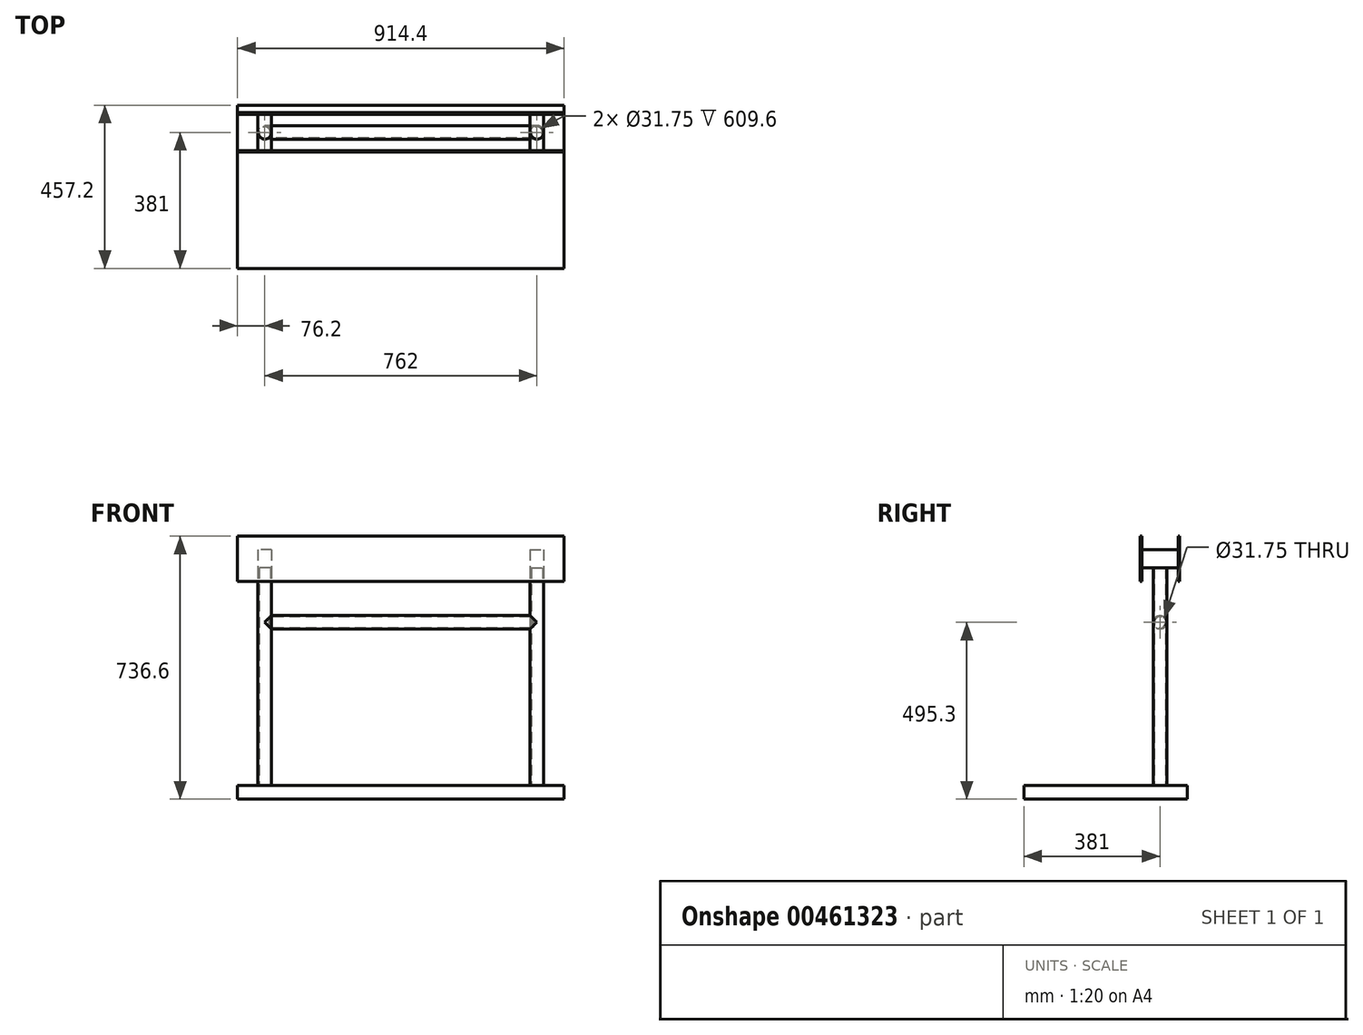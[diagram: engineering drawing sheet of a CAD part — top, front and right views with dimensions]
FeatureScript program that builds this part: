
annotation { "Feature Type Name" : "Feature", "Feature Type Description" : "" }
export const myFeature = defineFeature(function(context is Context, id is Id, definition is map)
    precondition{}
    {
        {
            var Q0;
            Q0=qCreatedBy(makeId("Top.planeOp"),FACE);
            var sketch = newSketch(context, id + "F0", { "sketchPlane" : qUnion([Q0])});
            skLineSegment(sketch, "E0.bottom", {"start": v(457.2, 228.6) * mm, "end": v(-457.2, 228.6) * mm});
            skLineSegment(sketch, "E0.top", {"start": v(457.2, -228.6) * mm, "end": v(-457.2, -228.6) * mm});
            skLineSegment(sketch, "E0.left", {"start": v(457.2, 228.6) * mm, "end": v(457.2, -228.6) * mm});
            skLineSegment(sketch, "E0.right", {"start": v(-457.2, 228.6) * mm, "end": v(-457.2, -228.6) * mm});
            skPoint(sketch, "E0.middle", {"position": v(0, 0) * mm});
            skSolve(sketch);
        }
        {
            var Q0;
            Q0 = qSketchRegion(id + "F0", true);
            extrude(context, id + "F1", {"entities" : qUnion([Q0]), "oppositeDirection" : true, "depth" : 38.1 * mm, "offsetDistance" : 25.4 * mm});
        }
        {
            var Q0;
            Q0=makeQuery(id+"F1.opExtrude","CAP_FACE",FACE,{"disambiguationData":[OSD([sQuery(id+"F0.wireOp",EDGE,"E0.bottom"),sQuery(id+"F0.wireOp",EDGE,"E0.top"),sQuery(id+"F0.wireOp",EDGE,"E0.left"),sQuery(id+"F0.wireOp",EDGE,"E0.right")])],"isStart":true});
            var sketch = newSketch(context, id + "F2", { "sketchPlane" : qUnion([Q0])});
            skCircle(sketch, "E1", {"center": v(-381, 152.4) * mm, "radius": 19.05 * mm});
            skCircle(sketch, "E2", {"center": v(-381, 152.4) * mm, "radius": 15.88 * mm});
            skSolve(sketch);
        }
        {
            var Q0;
            Q0 = qSketchRegion(id + "F2", true);
            extrude(context, id + "F3", {"entities" : qUnion([Q0]), "depth" : 609.6 * mm, "offsetDistance" : 25.4 * mm});
        }
        {
            var Q0;
            Q0=makeQuery(id+"F3.opExtrude","CAP_FACE",FACE,{"disambiguationData":[OSD([sQuery(id+"F2.wireOp",EDGE,"E1"),sQuery(id+"F2.wireOp",EDGE,"E2")])],"isStart":false});
            var sketch = newSketch(context, id + "F4", { "sketchPlane" : qUnion([Q0])});
            skLineSegment(sketch, "E3.bottom", {"start": v(-361.95, 101.6) * mm, "end": v(-400.05, 101.6) * mm});
            skLineSegment(sketch, "E3.top", {"start": v(-361.95, 203.2) * mm, "end": v(-400.05, 203.2) * mm});
            skLineSegment(sketch, "E3.left", {"start": v(-361.95, 101.6) * mm, "end": v(-361.95, 203.2) * mm});
            skLineSegment(sketch, "E3.right", {"start": v(-400.05, 101.6) * mm, "end": v(-400.05, 203.2) * mm});
            skPoint(sketch, "E3.middle", {"position": v(-381, 152.4) * mm});
            skSolve(sketch);
        }
        {
            var Q0;
            Q0 = qSketchRegion(id + "F4", true);
            extrude(context, id + "F5", {"entities" : qUnion([Q0]), "depth" : 50.8 * mm, "offsetDistance" : 25.4 * mm});
        }
        {
            var Q0;
            Q0=makeQuery(id+"F5.opExtrude","SWEPT_FACE",FACE,{"disambiguationData":[OSD([sQuery(id+"F4.wireOp",EDGE,"E3.bottom")])]});
            var Q1;
            Q1=makeQuery(id+"F5.opExtrude","SWEPT_FACE",FACE,{"disambiguationData":[OSD([sQuery(id+"F4.wireOp",EDGE,"E3.top")])]});
            cPlane(context, id + "F6", {"entities" : qUnion([Q0, Q1]), "cplaneType" : CPlaneType.MID_PLANE, "offset" : 25.4 * mm, "width" : 152.4 * mm, "height" : 152.4 * mm});
        }
        {
            var Q0;
            Q0=makeQuery(id+"F5.opExtrude","SWEPT_BODY",BODY,{"disambiguationData":[OSD([sQuery(id+"F4.wireOp",EDGE,"E3.bottom"),sQuery(id+"F4.wireOp",EDGE,"E3.top"),sQuery(id+"F4.wireOp",EDGE,"E3.left"),sQuery(id+"F4.wireOp",EDGE,"E3.right")])]});
            var Q1;
            Q1=makeQuery(id+"F3.opExtrude","SWEPT_BODY",BODY,{"disambiguationData":[OSD([sQuery(id+"F2.wireOp",EDGE,"E1"),sQuery(id+"F2.wireOp",EDGE,"E2")])]});
            var Q2;
            Q2=qCreatedBy(makeId("Right.planeOp"),FACE);
            mirror(context, id + "F7", {"entities" : qUnion([Q0, Q1]), "mirrorPlane" : qUnion([Q2])});
        }
        {
            var Q0;
            Q0=qCreatedBy(makeId("Right.planeOp"),FACE);
            var sketch = newSketch(context, id + "F8", { "sketchPlane" : qUnion([Q0])});
            skCircle(sketch, "E4", {"center": v(152.4, 457.2) * mm, "radius": 19.05 * mm});
            skCircle(sketch, "E5", {"center": v(152.4, 457.2) * mm, "radius": 15.88 * mm});
            skSolve(sketch);
        }
        {
            var Q0;
            Q0 = qSketchRegion(id + "F8", true);
            extrude(context, id + "F9", {"entities" : qUnion([Q0]), "endBound" : BoundingType.UP_TO_NEXT, "depth" : 25.4 * mm, "offsetDistance" : 25.4 * mm, "hasSecondDirection" : true, "secondDirectionBound" : SecondDirectionBoundingType.UP_TO_NEXT, "secondDirectionOppositeDirection" : true, "secondDirectionDepth" : 25.4 * mm});
        }
        {
            var Q0;
            Q0=makeQuery(id+"F5.opExtrude","SWEPT_FACE",FACE,{"disambiguationData":[OSD([sQuery(id+"F4.wireOp",EDGE,"E3.bottom")])]});
            var sketch = newSketch(context, id + "F10", { "sketchPlane" : qUnion([Q0])});
            skLineSegment(sketch, "E6.bottom", {"start": v(-457.2, 698.5) * mm, "end": v(457.2, 698.5) * mm});
            skLineSegment(sketch, "E6.top", {"start": v(-457.2, 571.5) * mm, "end": v(457.2, 571.5) * mm});
            skLineSegment(sketch, "E6.left", {"start": v(-457.2, 698.5) * mm, "end": v(-457.2, 571.5) * mm});
            skLineSegment(sketch, "E6.right", {"start": v(457.2, 698.5) * mm, "end": v(457.2, 571.5) * mm});
            skPoint(sketch, "E6.middle", {"position": v(0, 635) * mm});
            skSolve(sketch);
        }
        {
            var Q0;
            Q0 = qSketchRegion(id + "F10", true);
            extrude(context, id + "F11", {"entities" : qUnion([Q0]), "depth" : 4.76 * mm, "offsetDistance" : 25.4 * mm});
        }
        {
            var Q0;
            Q0=makeQuery(id+"F11.opExtrude","SWEPT_BODY",BODY,{"disambiguationData":[OSD([sQuery(id+"F10.wireOp",EDGE,"E6.bottom"),sQuery(id+"F10.wireOp",EDGE,"E6.top"),sQuery(id+"F10.wireOp",EDGE,"E6.left"),sQuery(id+"F10.wireOp",EDGE,"E6.right")])]});
            var Q1;
            Q1=qCreatedBy(id+"F6.planeOp",FACE);
            mirror(context, id + "F12", {"entities" : qUnion([Q0]), "mirrorPlane" : qUnion([Q1])});
        }
    });
